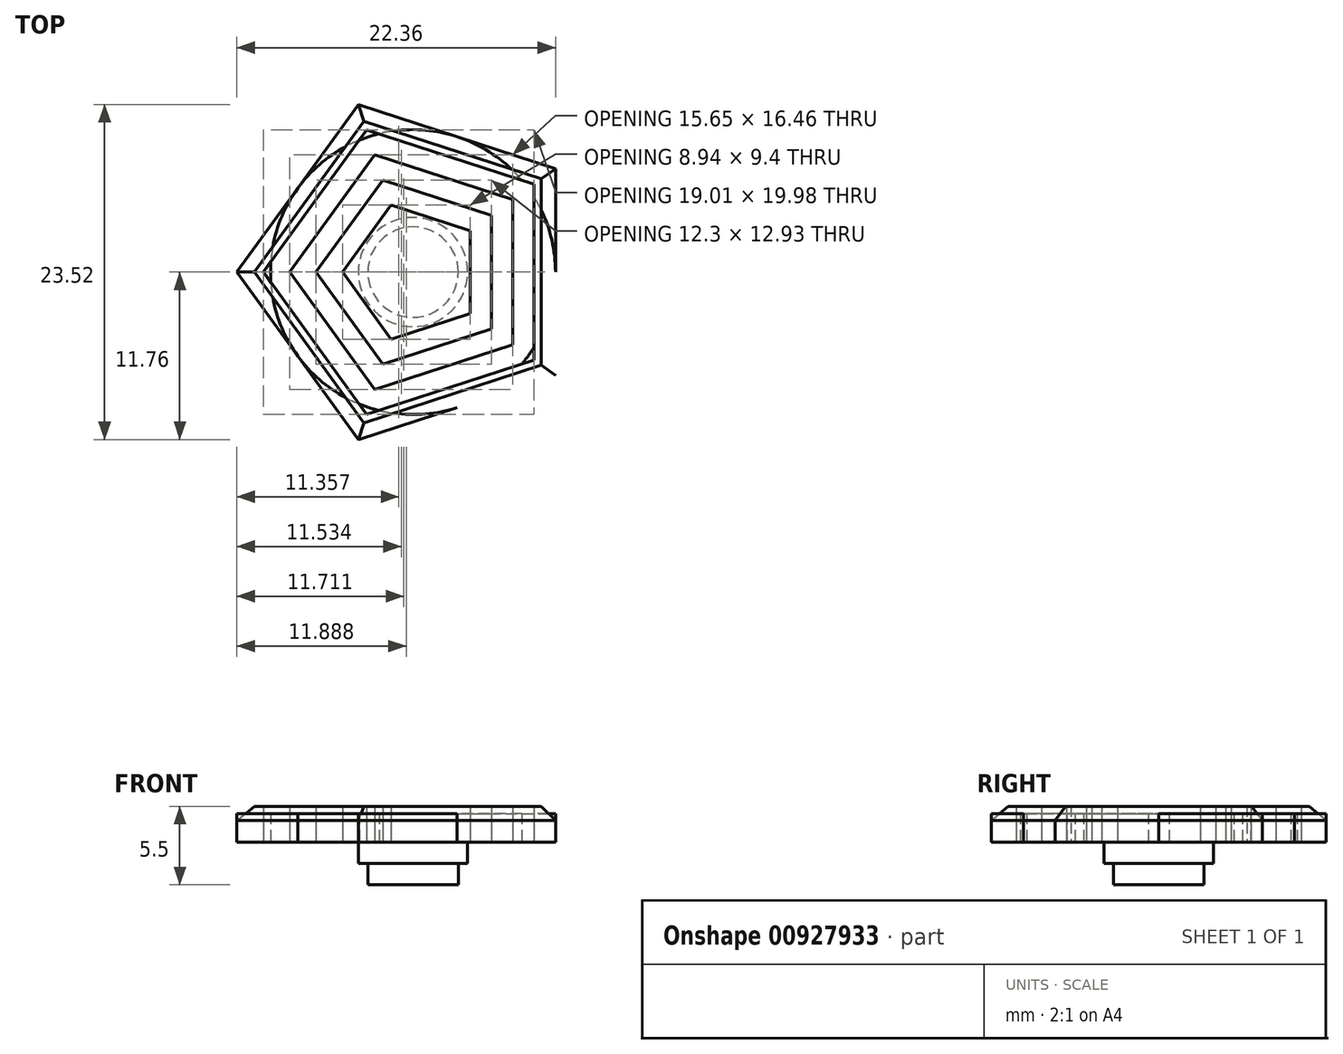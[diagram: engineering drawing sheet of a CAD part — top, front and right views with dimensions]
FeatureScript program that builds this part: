
annotation { "Feature Type Name" : "Feature", "Feature Type Description" : "" }
export const myFeature = defineFeature(function(context is Context, id is Id, definition is map)
    precondition{}
    {
        {
            var Q0;
            Q0=qCreatedBy(makeId("Top.planeOp"),FACE);
            var sketch = newSketch(context, id + "F0", { "sketchPlane" : qUnion([Q0])});
            skCircle(sketch, "E0", {"center": v(0, 0) * mm, "radius": 10 * mm});
            skCircle(sketch, "E1", {"center": v(0, 0) * mm, "radius": 3.17 * mm});
            skCircle(sketch, "E2", {"center": v(0, 0) * mm, "radius": 3.83 * mm});
            skCircle(sketch, "E3.cCircle", {"center": v(0, 0) * mm, "radius": 10 * mm, "construction": true});
            skLineSegment(sketch, "E3.0", {"start": v(10, 7.27) * mm, "end": v(10, -7.27) * mm});
            skLineSegment(sketch, "E3.1", {"start": v(10, -7.27) * mm, "end": v(-3.82, -11.76) * mm});
            skLineSegment(sketch, "E3.2", {"start": v(-3.82, -11.76) * mm, "end": v(-12.36, 0) * mm});
            skLineSegment(sketch, "E3.3", {"start": v(-12.36, 0) * mm, "end": v(-3.82, 11.76) * mm});
            skLineSegment(sketch, "E3.4", {"start": v(-3.82, 11.76) * mm, "end": v(10, 7.27) * mm});
            skPoint(sketch, "E3.0.midPoint", {"position": v(10, 0) * mm});
            skCircle(sketch, "E4.cCircle", {"center": v(0, 0) * mm, "radius": 5.5 * mm, "construction": true});
            skLineSegment(sketch, "E4.0", {"start": v(5.5, 4) * mm, "end": v(5.5, -4) * mm});
            skLineSegment(sketch, "E4.1", {"start": v(5.5, -4) * mm, "end": v(-2.1, -6.47) * mm});
            skLineSegment(sketch, "E4.2", {"start": v(-2.1, -6.47) * mm, "end": v(-6.8, 0) * mm});
            skLineSegment(sketch, "E4.3", {"start": v(-6.8, 0) * mm, "end": v(-2.1, 6.47) * mm});
            skLineSegment(sketch, "E4.4", {"start": v(-2.1, 6.47) * mm, "end": v(5.5, 4) * mm});
            skPoint(sketch, "E4.0.midPoint", {"position": v(5.5, 0) * mm});
            skCircle(sketch, "E5.cCircle", {"center": v(0, 0) * mm, "radius": 7 * mm, "construction": true});
            skLineSegment(sketch, "E5.0", {"start": v(7, 5.09) * mm, "end": v(7, -5.09) * mm});
            skLineSegment(sketch, "E5.1", {"start": v(7, -5.09) * mm, "end": v(-2.67, -8.23) * mm});
            skLineSegment(sketch, "E5.2", {"start": v(-2.67, -8.23) * mm, "end": v(-8.65, 0) * mm});
            skLineSegment(sketch, "E5.3", {"start": v(-8.65, 0) * mm, "end": v(-2.67, 8.23) * mm});
            skLineSegment(sketch, "E5.4", {"start": v(-2.67, 8.23) * mm, "end": v(7, 5.09) * mm});
            skPoint(sketch, "E5.0.midPoint", {"position": v(7, 0) * mm});
            skCircle(sketch, "E6.cCircle", {"center": v(0, 0) * mm, "radius": 8.5 * mm, "construction": true});
            skLineSegment(sketch, "E6.0", {"start": v(8.5, 6.18) * mm, "end": v(8.5, -6.18) * mm});
            skLineSegment(sketch, "E6.1", {"start": v(8.5, -6.18) * mm, "end": v(-3.25, -10) * mm});
            skLineSegment(sketch, "E6.2", {"start": v(-3.25, -10) * mm, "end": v(-10.5, 0) * mm});
            skLineSegment(sketch, "E6.3", {"start": v(-10.5, 0) * mm, "end": v(-3.25, 10) * mm});
            skLineSegment(sketch, "E6.4", {"start": v(-3.25, 10) * mm, "end": v(8.5, 6.18) * mm});
            skPoint(sketch, "E6.0.midPoint", {"position": v(8.5, 0) * mm});
            skCircle(sketch, "E7.cCircle", {"center": v(0, 0) * mm, "radius": 4 * mm, "construction": true});
            skLineSegment(sketch, "E7.0", {"start": v(4, 2.9) * mm, "end": v(4, -2.9) * mm});
            skLineSegment(sketch, "E7.1", {"start": v(4, -2.9) * mm, "end": v(-1.53, -4.7) * mm});
            skLineSegment(sketch, "E7.2", {"start": v(-1.53, -4.7) * mm, "end": v(-4.94, 0) * mm});
            skLineSegment(sketch, "E7.3", {"start": v(-4.94, 0) * mm, "end": v(-1.53, 4.7) * mm});
            skLineSegment(sketch, "E7.4", {"start": v(-1.53, 4.7) * mm, "end": v(4, 2.9) * mm});
            skPoint(sketch, "E7.0.midPoint", {"position": v(4, 0) * mm});
            skSolve(sketch);
        }
        {
            var Q0;
            Q0=makeQuery(id+"F0.imprint","IMPRINT",FACE,{"disambiguationData":[TD([[makeQuery(id+"F0.imprint","IMPRINT",EDGE,{"derivedFrom":sQuery(id+"F0.wireOp",EDGE,"E1")}),-1.0]])]});
            var Q1;
            Q1=makeQuery(id+"F0.imprint","IMPRINT",FACE,{"disambiguationData":[TD([[makeQuery(id+"F0.imprint","IMPRINT",EDGE,{"derivedFrom":sQuery(id+"F0.wireOp",EDGE,"E2")}),-1.0]])]});
            var Q2;
            Q2=makeQuery(id+"F0.imprint","IMPRINT",FACE,{"disambiguationData":[TD([[makeQuery(id+"F0.imprint","IMPRINT",EDGE,{"derivedFrom":sQuery(id+"F0.wireOp",EDGE,"E4.0")}),1.0]])]});
            var Q3;
            {var subQ0=sQuery(id+"F0.wireOp",EDGE,"E0");var subQ1=makeQuery(id+"F0.imprint","INTERSECT",VERTEX,{"derivedFrom":[subQ0,sQuery(id+"F0.wireOp",EDGE,"E3.2")]});Q3=makeQuery(id+"F0.imprint","IMPRINT",FACE,{"disambiguationData":[TD([[makeQuery(id+"F0.imprint","IMPRINT",EDGE,{"disambiguationData":[TD([[subQ1,1.0]])],"derivedFrom":subQ0}),1.0]])]});}
            var Q4;
            {var subQ0=sQuery(id+"F0.wireOp",EDGE,"E3.3");var subQ3=sQuery(id+"F0.wireOp",EDGE,"E0");var subQ5=makeQuery(id+"F0.imprint","INTERSECT",VERTEX,{"derivedFrom":[subQ3,subQ0]});Q4=makeQuery(id+"F0.imprint","IMPRINT",FACE,{"disambiguationData":[TD([[makeQuery(id+"F0.imprint","IMPRINT",EDGE,{"disambiguationData":[TD([[subQ5,-1.0]])],"derivedFrom":subQ3}),-1.0]])]});}
            var Q5;
            {var subQ0=sQuery(id+"F0.wireOp",EDGE,"E3.2");var subQ3=sQuery(id+"F0.wireOp",EDGE,"E0");var subQ5=makeQuery(id+"F0.imprint","INTERSECT",VERTEX,{"derivedFrom":[subQ3,subQ0]});Q5=makeQuery(id+"F0.imprint","IMPRINT",FACE,{"disambiguationData":[TD([[makeQuery(id+"F0.imprint","IMPRINT",EDGE,{"disambiguationData":[TD([[subQ5,-1.0]])],"derivedFrom":subQ3}),-1.0]])]});}
            var Q6;
            {var subQ0=sQuery(id+"F0.wireOp",EDGE,"E0");var subQ1=makeQuery(id+"F0.imprint","INTERSECT",VERTEX,{"derivedFrom":[subQ0,sQuery(id+"F0.wireOp",EDGE,"E3.1")]});Q6=makeQuery(id+"F0.imprint","IMPRINT",FACE,{"disambiguationData":[TD([[makeQuery(id+"F0.imprint","IMPRINT",EDGE,{"disambiguationData":[TD([[subQ1,1.0]])],"derivedFrom":subQ0}),1.0]])]});}
            var Q7;
            {var subQ0=sQuery(id+"F0.wireOp",EDGE,"E3.1");var subQ3=sQuery(id+"F0.wireOp",EDGE,"E0");var subQ9=makeQuery(id+"F0.imprint","INTERSECT",VERTEX,{"derivedFrom":[subQ3,subQ0]});Q7=makeQuery(id+"F0.imprint","IMPRINT",FACE,{"disambiguationData":[TD([[makeQuery(id+"F0.imprint","IMPRINT",EDGE,{"disambiguationData":[TD([[subQ9,-1.0]])],"derivedFrom":subQ3}),-1.0]])]});}
            var Q8;
            {var subQ0=sQuery(id+"F0.wireOp",EDGE,"E0");var subQ1=makeQuery(id+"F0.imprint","INTERSECT",VERTEX,{"derivedFrom":[subQ0,sQuery(id+"F0.wireOp",EDGE,"E3.0")]});Q8=makeQuery(id+"F0.imprint","IMPRINT",FACE,{"disambiguationData":[TD([[makeQuery(id+"F0.imprint","IMPRINT",EDGE,{"disambiguationData":[TD([[subQ1,-1.0]])],"derivedFrom":subQ0}),1.0]])]});}
            var Q9;
            {var subQ1=sQuery(id+"F0.wireOp",EDGE,"E3.0");var subQ3=sQuery(id+"F0.wireOp",EDGE,"E0");var subQ9=makeQuery(id+"F0.imprint","INTERSECT",VERTEX,{"derivedFrom":[subQ3,subQ1]});Q9=makeQuery(id+"F0.imprint","IMPRINT",FACE,{"disambiguationData":[TD([[makeQuery(id+"F0.imprint","IMPRINT",EDGE,{"disambiguationData":[TD([[subQ9,-1.0]])],"derivedFrom":subQ3}),-1.0]])]});}
            var Q10;
            {var subQ0=sQuery(id+"F0.wireOp",EDGE,"E3.4");var subQ3=sQuery(id+"F0.wireOp",EDGE,"E0");var subQ5=makeQuery(id+"F0.imprint","INTERSECT",VERTEX,{"derivedFrom":[subQ3,subQ0]});Q10=makeQuery(id+"F0.imprint","IMPRINT",FACE,{"disambiguationData":[TD([[makeQuery(id+"F0.imprint","IMPRINT",EDGE,{"disambiguationData":[TD([[subQ5,-1.0]])],"derivedFrom":subQ3}),-1.0]])]});}
            var Q11;
            {var subQ0=sQuery(id+"F0.wireOp",EDGE,"E0");var subQ1=makeQuery(id+"F0.imprint","INTERSECT",VERTEX,{"derivedFrom":[subQ0,sQuery(id+"F0.wireOp",EDGE,"E3.3")]});Q11=makeQuery(id+"F0.imprint","IMPRINT",FACE,{"disambiguationData":[TD([[makeQuery(id+"F0.imprint","IMPRINT",EDGE,{"disambiguationData":[TD([[subQ1,1.0]])],"derivedFrom":subQ0}),1.0]])]});}
            var Q12;
            {var subQ0=sQuery(id+"F0.wireOp",EDGE,"E0");var subQ1=makeQuery(id+"F0.imprint","INTERSECT",VERTEX,{"derivedFrom":[subQ0,sQuery(id+"F0.wireOp",EDGE,"E3.4")]});Q12=makeQuery(id+"F0.imprint","IMPRINT",FACE,{"disambiguationData":[TD([[makeQuery(id+"F0.imprint","IMPRINT",EDGE,{"disambiguationData":[TD([[subQ1,1.0]])],"derivedFrom":subQ0}),1.0]])]});}
            var Q13;
            Q13=makeQuery(id+"F0.imprint","IMPRINT",FACE,{"disambiguationData":[TD([[makeQuery(id+"F0.imprint","IMPRINT",EDGE,{"derivedFrom":sQuery(id+"F0.wireOp",EDGE,"E1")}),1.0]])]});
            extrude(context, id + "F1", {"entities" : qUnion([Q0, Q1, Q2, Q3, Q4, Q5, Q6, Q7, Q8, Q9, Q10, Q11, Q12, Q13]), "depth" : 2.5 * mm, "offsetDistance" : 25 * mm});
        }
        {
            var Q0;
            Q0=makeQuery(id+"F1.opExtrude","CAP_FACE",FACE,{"disambiguationData":[OSD([sQuery(id+"F0.wireOp",EDGE,"E0")])],"isStart":false});
            var Q1;
            Q1=makeQuery(id+"F1.opExtrude","CAP_EDGE",EDGE,{"disambiguationData":[OSD([sQuery(id+"F0.wireOp",EDGE,"E3.1")])],"isStart":false});
            var Q2;
            Q2=makeQuery(id+"F1.opExtrude","CAP_EDGE",EDGE,{"disambiguationData":[OSD([sQuery(id+"F0.wireOp",EDGE,"E3.2")])],"isStart":false});
            var Q3;
            Q3=makeQuery(id+"F1.opExtrude","CAP_EDGE",EDGE,{"disambiguationData":[OSD([sQuery(id+"F0.wireOp",EDGE,"E3.3")])],"isStart":false});
            var Q4;
            Q4=makeQuery(id+"F1.opExtrude","CAP_EDGE",EDGE,{"disambiguationData":[OSD([sQuery(id+"F0.wireOp",EDGE,"E3.4")])],"isStart":false});
            var Q5;
            Q5=makeQuery(id+"F1.opExtrude","CAP_EDGE",EDGE,{"disambiguationData":[OSD([sQuery(id+"F0.wireOp",EDGE,"E3.0")])],"isStart":false});
            chamfer(context, id + "F2", {"entities" : qUnion([Q0, Q1, Q2, Q3, Q4, Q5]), "width" : 1 * mm, "tangentPropagation" : true});
        }
        {
            var Q0;
            Q0=makeQuery(id+"F0.imprint","IMPRINT",FACE,{"disambiguationData":[TD([[makeQuery(id+"F0.imprint","IMPRINT",EDGE,{"derivedFrom":sQuery(id+"F0.wireOp",EDGE,"E1")}),1.0]])]});
            extrude(context, id + "F3", {"entities" : qUnion([Q0]), "operationType" : NewBodyOperationType.ADD, "oppositeDirection" : true, "depth" : 3 * mm, "offsetDistance" : 25 * mm});
        }
        {
            var Q0;
            Q0=makeQuery(id+"F0.imprint","IMPRINT",FACE,{"disambiguationData":[TD([[makeQuery(id+"F0.imprint","IMPRINT",EDGE,{"derivedFrom":sQuery(id+"F0.wireOp",EDGE,"E1")}),-1.0]])]});
            extrude(context, id + "F4", {"entities" : qUnion([Q0]), "operationType" : NewBodyOperationType.ADD, "oppositeDirection" : true, "depth" : 1.5 * mm, "offsetDistance" : 25 * mm});
        }
        {
            var Q0;
            Q0=makeQuery(id+"F0.imprint","IMPRINT",FACE,{"disambiguationData":[TD([[makeQuery(id+"F0.imprint","IMPRINT",EDGE,{"derivedFrom":sQuery(id+"F0.wireOp",EDGE,"E5.0")}),1.0]])]});
            var Q1;
            {var subQ0=sQuery(id+"F0.wireOp",EDGE,"E6.3");var subQ1=sQuery(id+"F0.wireOp",EDGE,"E0");var subQ2=makeQuery(id+"F0.imprint","INTERSECT",VERTEX,{"disambiguationData":[OD(1.0)],"derivedFrom":[subQ1,subQ0]});Q1=makeQuery(id+"F0.imprint","IMPRINT",FACE,{"disambiguationData":[TD([[makeQuery(id+"F0.imprint","IMPRINT",EDGE,{"disambiguationData":[TD([[subQ2,-1.0]])],"derivedFrom":subQ1}),-1.0]])]});}
            var Q2;
            {var subQ0=sQuery(id+"F0.wireOp",EDGE,"E6.4");var subQ1=sQuery(id+"F0.wireOp",EDGE,"E0");var subQ2=makeQuery(id+"F0.imprint","INTERSECT",VERTEX,{"disambiguationData":[OD(1.0)],"derivedFrom":[subQ1,subQ0]});Q2=makeQuery(id+"F0.imprint","IMPRINT",FACE,{"disambiguationData":[TD([[makeQuery(id+"F0.imprint","IMPRINT",EDGE,{"disambiguationData":[TD([[subQ2,-1.0]])],"derivedFrom":subQ1}),-1.0]])]});}
            var Q3;
            {var subQ0=sQuery(id+"F0.wireOp",EDGE,"E6.0");var subQ1=sQuery(id+"F0.wireOp",EDGE,"E0");var subQ2=makeQuery(id+"F0.imprint","INTERSECT",VERTEX,{"disambiguationData":[OD(0.0)],"derivedFrom":[subQ1,subQ0]});Q3=makeQuery(id+"F0.imprint","IMPRINT",FACE,{"disambiguationData":[TD([[makeQuery(id+"F0.imprint","IMPRINT",EDGE,{"disambiguationData":[TD([[subQ2,-1.0]])],"derivedFrom":subQ1}),-1.0]])]});}
            var Q4;
            {var subQ0=sQuery(id+"F0.wireOp",EDGE,"E6.1");var subQ1=sQuery(id+"F0.wireOp",EDGE,"E0");var subQ2=makeQuery(id+"F0.imprint","INTERSECT",VERTEX,{"disambiguationData":[OD(1.0)],"derivedFrom":[subQ1,subQ0]});Q4=makeQuery(id+"F0.imprint","IMPRINT",FACE,{"disambiguationData":[TD([[makeQuery(id+"F0.imprint","IMPRINT",EDGE,{"disambiguationData":[TD([[subQ2,-1.0]])],"derivedFrom":subQ1}),-1.0]])]});}
            var Q5;
            {var subQ0=sQuery(id+"F0.wireOp",EDGE,"E6.2");var subQ1=sQuery(id+"F0.wireOp",EDGE,"E0");var subQ2=makeQuery(id+"F0.imprint","INTERSECT",VERTEX,{"disambiguationData":[OD(1.0)],"derivedFrom":[subQ1,subQ0]});Q5=makeQuery(id+"F0.imprint","IMPRINT",FACE,{"disambiguationData":[TD([[makeQuery(id+"F0.imprint","IMPRINT",EDGE,{"disambiguationData":[TD([[subQ2,-1.0]])],"derivedFrom":subQ1}),-1.0]])]});}
            var Q6;
            Q6=makeQuery(id+"F0.imprint","IMPRINT",FACE,{"disambiguationData":[TD([[makeQuery(id+"F0.imprint","IMPRINT",EDGE,{"derivedFrom":sQuery(id+"F0.wireOp",EDGE,"E4.0")}),-1.0]])]});
            extrude(context, id + "F5", {"entities" : qUnion([Q0, Q1, Q2, Q3, Q4, Q5, Q6]), "depth" : 2 * mm, "offsetDistance" : 25 * mm});
        }
    });
